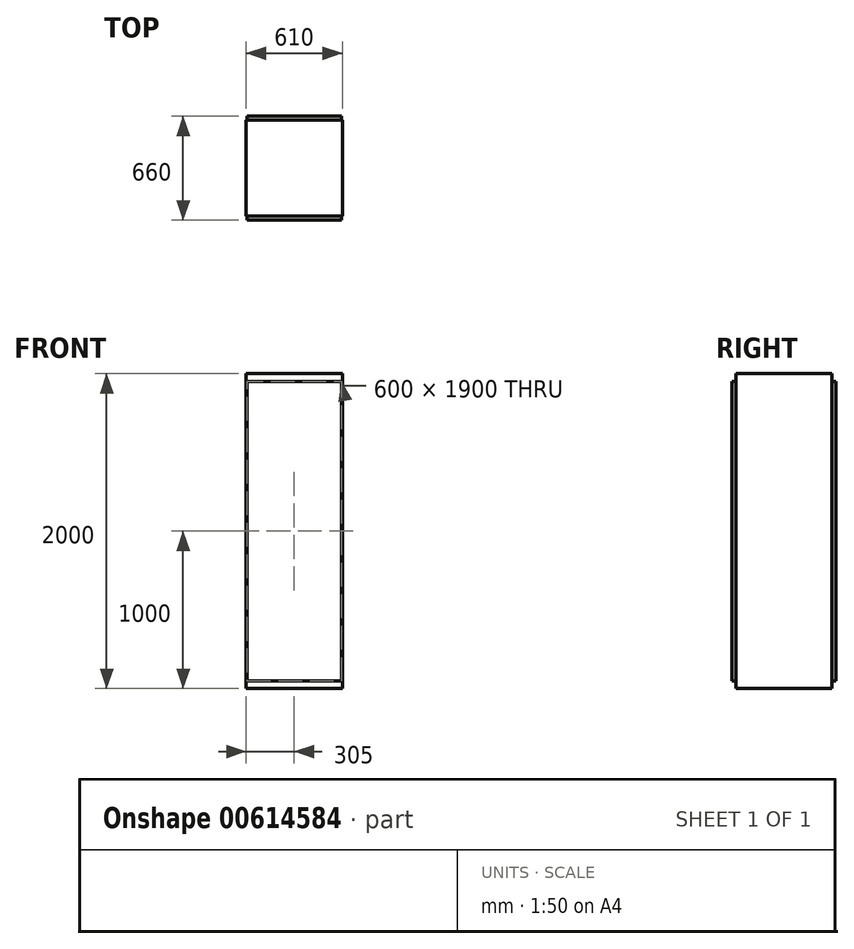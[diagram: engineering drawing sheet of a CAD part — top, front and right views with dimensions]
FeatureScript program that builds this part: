
annotation { "Feature Type Name" : "Feature", "Feature Type Description" : "" }
export const myFeature = defineFeature(function(context is Context, id is Id, definition is map)
    precondition{}
    {
        {
            var Q0;
            Q0=qCreatedBy(makeId("Top.planeOp"),FACE);
            var sketch = newSketch(context, id + "F0", { "sketchPlane" : qUnion([Q0])});
            skLineSegment(sketch, "E0.bottom", {"start": v(0, 0) * mm, "end": v(610, 0) * mm});
            skLineSegment(sketch, "E0.top", {"start": v(0, -610) * mm, "end": v(610, -610) * mm});
            skLineSegment(sketch, "E0.left", {"start": v(0, 0) * mm, "end": v(0, -610) * mm});
            skLineSegment(sketch, "E0.right", {"start": v(610, 0) * mm, "end": v(610, -610) * mm});
            skSolve(sketch);
        }
        {
            var Q0;
            Q0=makeQuery(id+"F0.imprint","IMPRINT",FACE,{"disambiguationData":[TD([[makeQuery(id+"F0.imprint","IMPRINT",EDGE,{"derivedFrom":sQuery(id+"F0.wireOp",EDGE,"E0.bottom")}),-1.0]])]});
            extrude(context, id + "F1", {"entities" : qUnion([Q0]), "depth" : 2000 * mm, "offsetDistance" : 25 * mm});
        }
        {
            var Q0;
            Q0=makeQuery(id+"F1.opExtrude","SWEPT_FACE",FACE,{"disambiguationData":[OSD([sQuery(id+"F0.wireOp",EDGE,"E0.top")])]});
            var sketch = newSketch(context, id + "F2", { "sketchPlane" : qUnion([Q0])});
            skLineSegment(sketch, "E1.bottom", {"start": v(605, 1950) * mm, "end": v(5, 1950) * mm});
            skLineSegment(sketch, "E1.top", {"start": v(605, 50) * mm, "end": v(5, 50) * mm});
            skLineSegment(sketch, "E1.left", {"start": v(605, 1950) * mm, "end": v(605, 50) * mm});
            skLineSegment(sketch, "E1.right", {"start": v(5, 1950) * mm, "end": v(5, 50) * mm});
            skPoint(sketch, "E1.middle", {"position": v(305, 1000) * mm});
            skPoint(sketch, "E1.middle.positionSnap0", {"position": v(0, 1000) * mm});
            skPoint(sketch, "E1.middle.positionSnap1", {"position": v(305, 2000) * mm});
            skPoint(sketch, "E1.centerSnap0", {"position": v(0, 1000) * mm});
            skPoint(sketch, "E1.centerSnap1", {"position": v(305, 2000) * mm});
            skSolve(sketch);
        }
        {
            var Q0;
            Q0=makeQuery(id+"F2.imprint","IMPRINT",FACE,{"disambiguationData":[TD([[makeQuery(id+"F2.imprint","IMPRINT",EDGE,{"derivedFrom":sQuery(id+"F2.wireOp",EDGE,"E1.bottom")}),1.0]])]});
            extrude(context, id + "F3", {"entities" : qUnion([Q0]), "operationType" : NewBodyOperationType.ADD, "depth" : 25 * mm, "offsetDistance" : 25 * mm});
        }
        {
            var Q0;
            Q0=makeQuery(id+"F1.opExtrude","CAP_EDGE",EDGE,{"disambiguationData":[OSD([sQuery(id+"F0.wireOp",EDGE,"E0.left")])],"isStart":false});
            cPoint(context, id + "F4", {"entities" : qUnion([Q0]), "parameter" : 0.5});
        }
        {
            var Q0;
            Q0=makeQuery(id+"F1.opExtrude","CAP_EDGE",EDGE,{"disambiguationData":[OSD([sQuery(id+"F0.wireOp",EDGE,"E0.right")])],"isStart":false});
            cPoint(context, id + "F5", {"entities" : qUnion([Q0]), "parameter" : 0.5});
        }
        {
            var Q0;
            Q0=makeQuery(id+"F1.opExtrude","CAP_EDGE",EDGE,{"disambiguationData":[OSD([sQuery(id+"F0.wireOp",EDGE,"E0.right")])],"isStart":true});
            cPoint(context, id + "F6", {"entities" : qUnion([Q0]), "parameter" : 0.5});
        }
        {
            var Q0;
            Q0 = qCreatedBy(id + "F4" ,VERTEX);
            var Q1;
            Q1 = qCreatedBy(id + "F5" ,VERTEX);
            var Q2;
            Q2 = qCreatedBy(id + "F6" ,VERTEX);
            cPlane(context, id + "F7", {"entities" : qUnion([Q0, Q1, Q2]), "cplaneType" : CPlaneType.THREE_POINT, "offset" : 25 * mm, "width" : 150 * mm, "height" : 150 * mm});
        }
        {
            var Q0;
            Q0=makeQuery(id+"F1.opExtrude","SWEPT_BODY",BODY,{"disambiguationData":[OSD([sQuery(id+"F0.wireOp",EDGE,"E0.bottom"),sQuery(id+"F0.wireOp",EDGE,"E0.top"),sQuery(id+"F0.wireOp",EDGE,"E0.left"),sQuery(id+"F0.wireOp",EDGE,"E0.right")])]});
            var Q1;
            Q1=qCreatedBy(id+"F7.planeOp",FACE);
            mirror(context, id + "F8", {"operationType" : NewBodyOperationType.ADD, "entities" : qUnion([Q0]), "mirrorPlane" : qUnion([Q1])});
        }
    });
